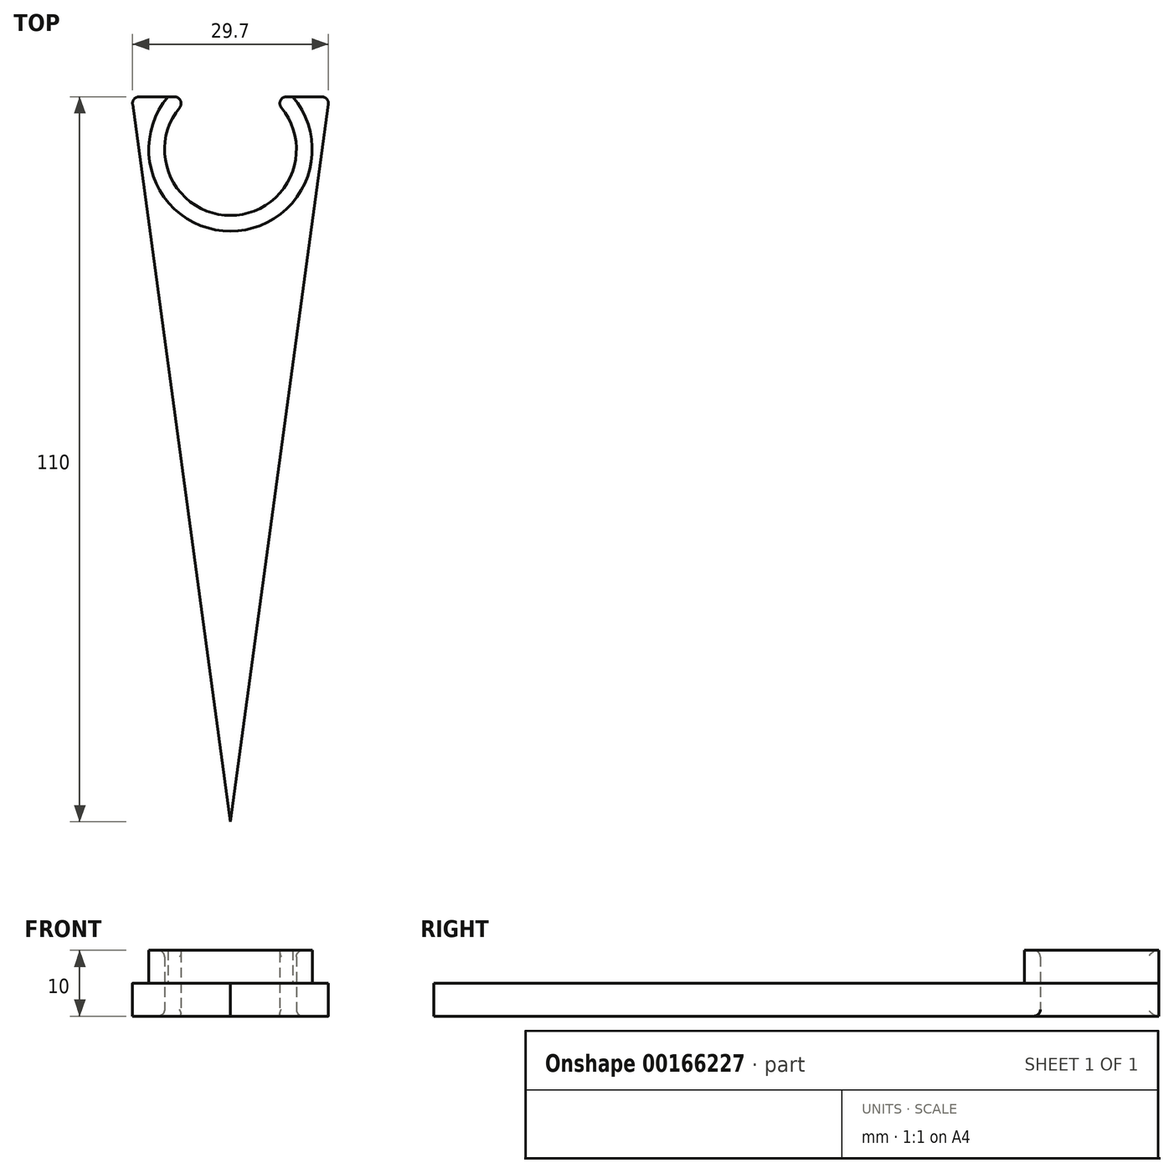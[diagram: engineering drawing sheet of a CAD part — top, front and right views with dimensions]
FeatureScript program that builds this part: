
annotation { "Feature Type Name" : "Feature", "Feature Type Description" : "" }
export const myFeature = defineFeature(function(context is Context, id is Id, definition is map)
    precondition{}
    {
        {
            var Q0;
            Q0=qCreatedBy(makeId("Top.planeOp"),FACE);
            var sketch = newSketch(context, id + "F0", { "sketchPlane" : qUnion([Q0])});
            skLineSegment(sketch, "E0", {"start": v(0, -110) * mm, "end": v(-15, 0) * mm});
            skLineSegment(sketch, "E1", {"start": v(-15, 0) * mm, "end": v(15, 0) * mm});
            skLineSegment(sketch, "E2", {"start": v(15, 0) * mm, "end": v(0, -110) * mm});
            skCircle(sketch, "E3", {"center": v(0, -8) * mm, "radius": 10 * mm});
            skSolve(sketch);
        }
        {
            var Q0;
            {var subQ4=sQuery(id+"F0.wireOp",EDGE,"E0");Q0=makeQuery(id+"F0.imprint","IMPRINT",FACE,{"disambiguationData":[TD([[makeQuery(id+"F0.imprint","IMPRINT",EDGE,{"derivedFrom":subQ4}),-1.0]])]});}
            extrude(context, id + "F1", {"entities" : qUnion([Q0]), "depth" : 5 * mm});
        }
        {
            var Q0;
            Q0=makeQuery(id+"F1.opExtrude","CAP_FACE",FACE,{"disambiguationData":[OSD([sQuery(id+"F0.wireOp",EDGE,"E0"),sQuery(id+"F0.wireOp",EDGE,"E1"),sQuery(id+"F0.wireOp",EDGE,"E2"),sQuery(id+"F0.wireOp",EDGE,"E3")])],"isStart":false});
            var sketch = newSketch(context, id + "F2", { "sketchPlane" : qUnion([Q0])});
            skArc(sketch, "E4.0", {"start": v(-6, 0) * mm, "mid": v(0, -18) * mm, "end": v(6, 0) * mm});
            skArc(sketch, "E5.0", {"start": v(-9.47, 0) * mm, "mid": v(0, -20.4) * mm, "end": v(9.47, 0) * mm});
            skSolve(sketch);
        }
        {
            var Q0;
            {var subQ0=sQuery(id+"F2.wireOp",EDGE,"E4.0");Q0=makeQuery(id+"F2.imprint","IMPRINT",FACE,{"disambiguationData":[TD([[makeQuery(id+"F2.imprint","IMPRINT",EDGE,{"derivedFrom":subQ0}),-1.0]])]});}
            extrude(context, id + "F3", {"entities" : qUnion([Q0]), "operationType" : NewBodyOperationType.ADD, "depth" : 5 * mm});
        }
        {
            var Q0;
            {var subQ0=sQuery(id+"F2.wireOp",EDGE,"E4.0");var subQ1=sQuery(id+"F0.wireOp",EDGE,"E1");var subQ2=sQuery(id+"F0.wireOp",EDGE,"E3");var subQ3=makeQuery(id+"F0.imprint","INTERSECT",VERTEX,{"disambiguationData":[OD(0.0)],"derivedFrom":[subQ1,subQ2]});Q0=makeQuery(id+"F3.boolean.opBoolean","MERGE",EDGE,{"derivedFrom":[makeQuery(id+"F1.opExtrude","SWEPT_EDGE",EDGE,{"disambiguationData":[OSD([subQ1,subQ2]),TDD([subQ3])]}),makeQuery(id+"F3.opExtrude","SWEPT_EDGE",EDGE,{"disambiguationData":[OSD([subQ1,subQ0]),TDD([makeQuery(id+"F2.imprint","INTERSECT",VERTEX,{"derivedFrom":[makeQuery(id+"F1.opExtrude","CAP_EDGE",EDGE,{"disambiguationData":[OSD([subQ1]),TDD([makeQuery(id+"F0.imprint","IMPRINT",EDGE,{"disambiguationData":[TD([[makeQuery(id+"F0.imprint","INTERSECT",VERTEX,{"derivedFrom":[sQuery(id+"F0.wireOp",EDGE,"E0"),subQ1]}),-1.0]])],"derivedFrom":subQ1})])],"isStart":false}),subQ0]})])]})]});}
            var Q1;
            {var subQ0=sQuery(id+"F2.wireOp",EDGE,"E4.0");var subQ1=sQuery(id+"F0.wireOp",EDGE,"E1");var subQ2=sQuery(id+"F0.wireOp",EDGE,"E3");var subQ3=makeQuery(id+"F0.imprint","INTERSECT",VERTEX,{"disambiguationData":[OD(1.0)],"derivedFrom":[subQ1,subQ2]});Q1=makeQuery(id+"F3.boolean.opBoolean","MERGE",EDGE,{"derivedFrom":[makeQuery(id+"F1.opExtrude","SWEPT_EDGE",EDGE,{"disambiguationData":[OSD([subQ1,subQ2]),TDD([subQ3])]}),makeQuery(id+"F3.opExtrude","SWEPT_EDGE",EDGE,{"disambiguationData":[OSD([subQ1,subQ0]),TDD([makeQuery(id+"F2.imprint","INTERSECT",VERTEX,{"derivedFrom":[makeQuery(id+"F1.opExtrude","CAP_EDGE",EDGE,{"disambiguationData":[OSD([subQ1]),TDD([makeQuery(id+"F0.imprint","IMPRINT",EDGE,{"disambiguationData":[TD([[makeQuery(id+"F0.imprint","INTERSECT",VERTEX,{"derivedFrom":[subQ1,sQuery(id+"F0.wireOp",EDGE,"E2")]}),1.0]])],"derivedFrom":subQ1})])],"isStart":false}),subQ0]})])]})]});}
            var Q2;
            Q2=makeQuery(id+"F3.opExtrude","CAP_EDGE",EDGE,{"disambiguationData":[OSD([sQuery(id+"F2.wireOp",EDGE,"E4.0")])],"isStart":false});
            var Q3;
            Q3=makeQuery(id+"F1.opExtrude","CAP_EDGE",EDGE,{"disambiguationData":[OSD([sQuery(id+"F0.wireOp",EDGE,"E3")])],"isStart":true});
            var Q4;
            Q4=makeQuery(id+"F3.opExtrude","CAP_EDGE",EDGE,{"disambiguationData":[OSD([sQuery(id+"F2.wireOp",EDGE,"E5.0")])],"isStart":true});
            var Q5;
            Q5=makeQuery(id+"F1.opExtrude","SWEPT_EDGE",EDGE,{"disambiguationData":[OSD([sQuery(id+"F0.wireOp",EDGE,"E0"),sQuery(id+"F0.wireOp",EDGE,"E1")])]});
            var Q6;
            Q6=makeQuery(id+"F1.opExtrude","SWEPT_EDGE",EDGE,{"disambiguationData":[OSD([sQuery(id+"F0.wireOp",EDGE,"E1"),sQuery(id+"F0.wireOp",EDGE,"E2")])]});
            fillet(context, id + "F4", {"entities" : qUnion([Q0, Q1, Q2, Q3, Q4, Q5, Q6]), "radius" : 1 * mm, "tangentPropagation" : true, "allowEdgeOverflow" : false});
        }
    });
